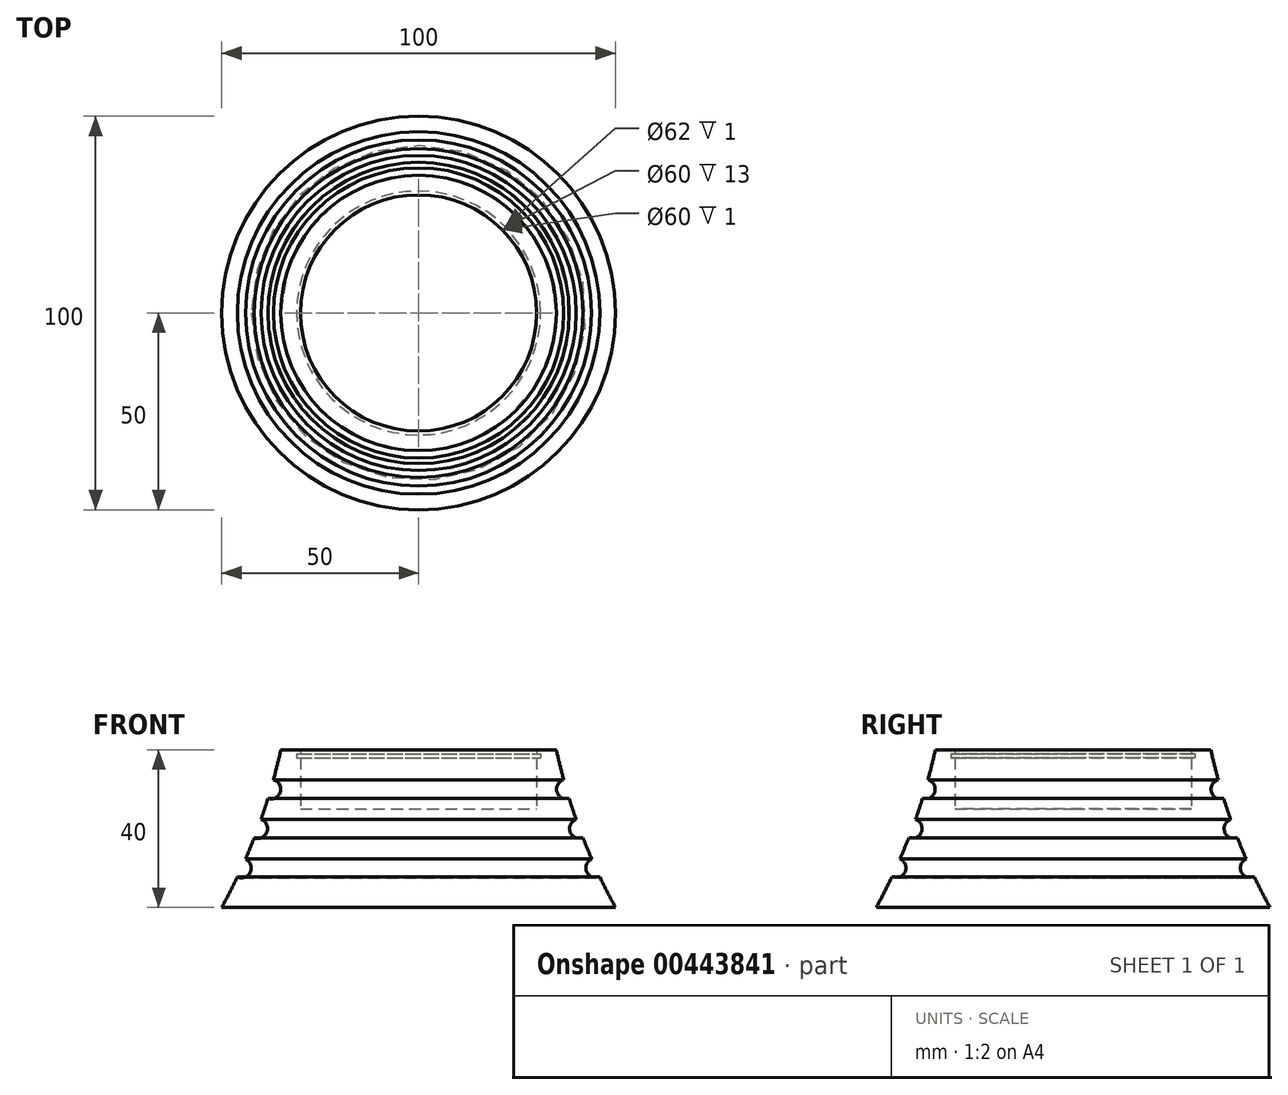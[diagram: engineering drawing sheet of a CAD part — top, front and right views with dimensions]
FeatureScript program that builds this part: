
annotation { "Feature Type Name" : "Feature", "Feature Type Description" : "" }
export const myFeature = defineFeature(function(context is Context, id is Id, definition is map)
    precondition{}
    {
        {
            var Q0;
            Q0=qCreatedBy(makeId("Front.planeOp"),FACE);
            var sketch = newSketch(context, id + "F0", { "sketchPlane" : qUnion([Q0])});
            skLineSegment(sketch, "E0", {"start": v(0, 0) * mm, "end": v(0, 25) * mm});
            skLineSegment(sketch, "E1", {"start": v(0, 25) * mm, "end": v(30, 25) * mm});
            skLineSegment(sketch, "E2", {"start": v(30, 25) * mm, "end": v(30, 38) * mm});
            skLineSegment(sketch, "E3", {"start": v(30, 40) * mm, "end": v(35, 40) * mm});
            skLineSegment(sketch, "E4", {"start": v(0, 0) * mm, "end": v(50, 0) * mm});
            skArc(sketch, "E5", {"start": v(35, 40) * mm, "mid": v(35.89, 36.2) * mm, "end": v(36.87, 32.4) * mm});
            skLineSegment(sketch, "E6.bottom", {"start": v(30, 39) * mm, "end": v(31, 39) * mm});
            skLineSegment(sketch, "E6.top", {"start": v(30, 38) * mm, "end": v(31, 38) * mm});
            skLineSegment(sketch, "E6.right", {"start": v(31, 39) * mm, "end": v(31, 38) * mm});
            skLineSegment(sketch, "E7.trimOffspring", {"start": v(30, 39) * mm, "end": v(30, 40) * mm});
            skArc(sketch, "E8", {"start": v(40.02, 22.35) * mm, "mid": v(38.52, 19.13) * mm, "end": v(41.76, 17.66) * mm});
            skArc(sketch, "E9", {"start": v(43.97, 12.28) * mm, "mid": v(42.72, 8.96) * mm, "end": v(46.05, 7.73) * mm});
            skPoint(sketch, "E10.center.orphan", {"position": v(37.56, 30) * mm});
            skArc(sketch, "E11", {"start": v(36.87, 32.4) * mm, "mid": v(35.16, 29.3) * mm, "end": v(38.28, 27.6) * mm});
            skArc(sketch, "E12.trimOffspring", {"start": v(38.28, 27.6) * mm, "mid": v(39.12, 24.97) * mm, "end": v(40.02, 22.35) * mm});
            skArc(sketch, "E13.trimOffspring", {"start": v(41.76, 17.66) * mm, "mid": v(42.84, 14.96) * mm, "end": v(43.97, 12.28) * mm});
            skArc(sketch, "E14.trimOffspring", {"start": v(46.05, 7.73) * mm, "mid": v(47.97, 3.84) * mm, "end": v(50, 0) * mm});
            skSolve(sketch);
        }
        {
            var Q0;
            Q0 = qSketchRegion(id + "F0", true);
            var Q1;
            Q1=sQuery(id+"F0.wireOp",EDGE,"E0");
            revolve(context, id + "F1", {"entities" : qUnion([Q0]), "axis" : qUnion([Q1]), "revolveType" : RevolveType.FULL});
        }
    });
